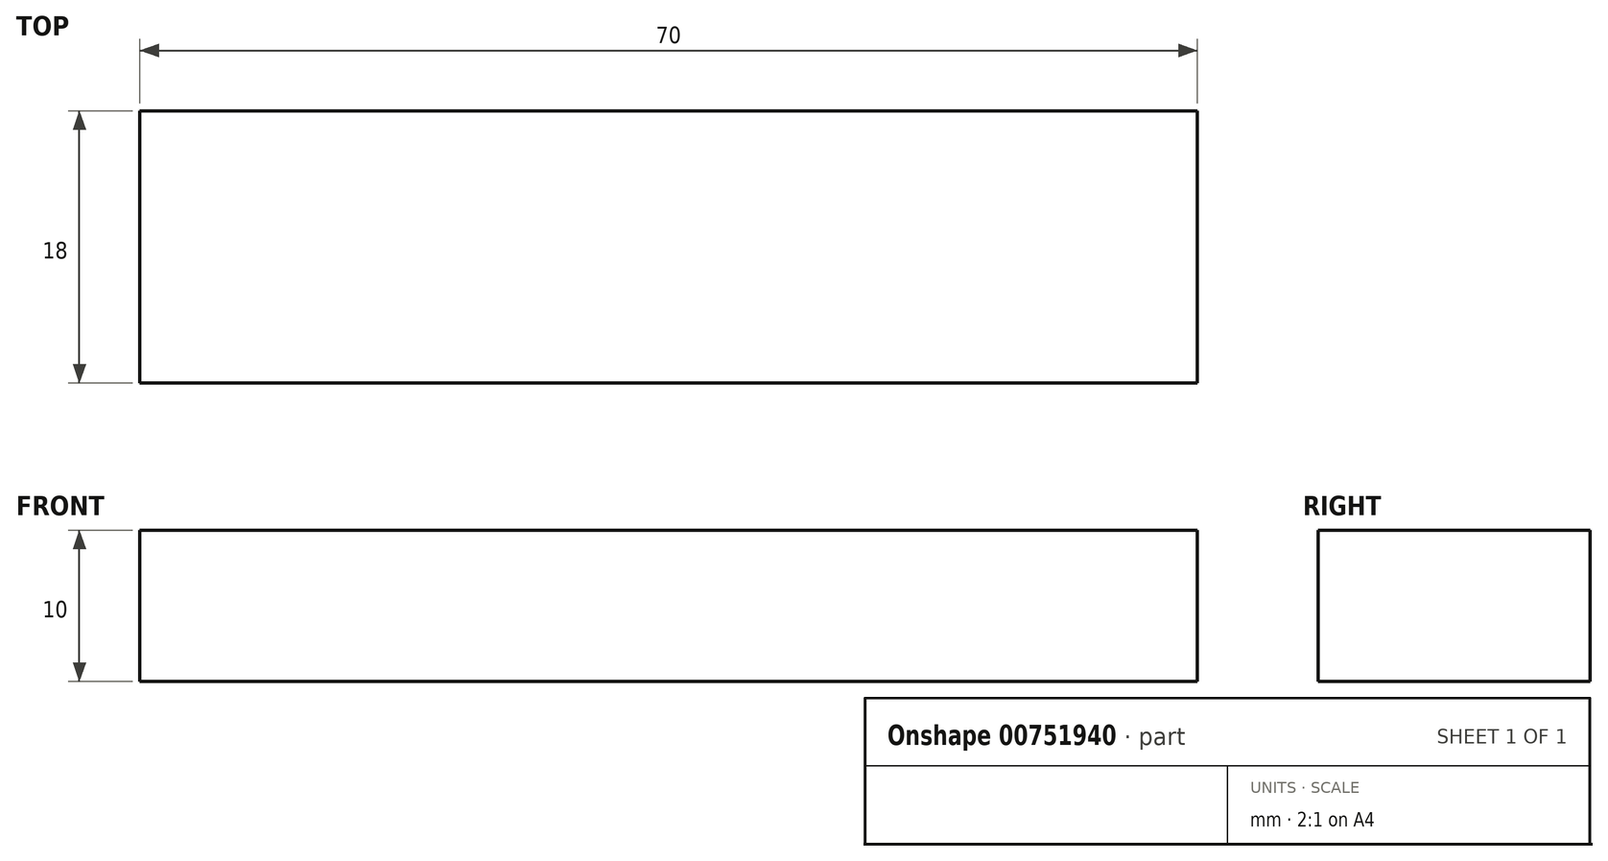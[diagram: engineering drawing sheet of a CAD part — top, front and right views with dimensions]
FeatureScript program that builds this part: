
annotation { "Feature Type Name" : "Feature", "Feature Type Description" : "" }
export const myFeature = defineFeature(function(context is Context, id is Id, definition is map)
    precondition{}
    {
        {
            var Q0;
            Q0=qCreatedBy(makeId("Top.planeOp"),FACE);
            var sketch = newSketch(context, id + "F0", { "sketchPlane" : qUnion([Q0])});
            skLineSegment(sketch, "E0.bottom", {"start": v(35, 9) * mm, "end": v(-35, 9) * mm});
            skLineSegment(sketch, "E0.top", {"start": v(35, -9) * mm, "end": v(-35, -9) * mm});
            skLineSegment(sketch, "E0.left", {"start": v(35, 9) * mm, "end": v(35, -9) * mm});
            skLineSegment(sketch, "E0.right", {"start": v(-35, 9) * mm, "end": v(-35, -9) * mm});
            skPoint(sketch, "E0.middle", {"position": v(0, 0) * mm});
            skSolve(sketch);
        }
        {
            var Q0;
            Q0=makeQuery(id+"F0.imprint","IMPRINT",FACE,{"disambiguationData":[TD([[makeQuery(id+"F0.imprint","IMPRINT",EDGE,{"derivedFrom":sQuery(id+"F0.wireOp",EDGE,"E0.bottom")}),1.0]])]});
            extrude(context, id + "F1", {"entities" : qUnion([Q0]), "depth" : 10 * mm, "offsetDistance" : 25 * mm});
        }
    });
